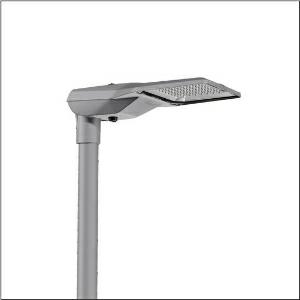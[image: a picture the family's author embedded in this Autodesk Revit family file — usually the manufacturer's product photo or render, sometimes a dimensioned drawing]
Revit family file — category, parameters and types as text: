
# Revit family: streetlight_sl_21_midi___st1_0a_5xe3d63t08nb_4f09
name_source: partatom
category: Lighting Fixtures
units: mm (PartAtom-declared; Revit-internal decimal feet)

## family parameters
Cut with Voids When Loaded = No
Host = Face
Light Source = No
Part Type = Normal
Room Calculation Point = No
Round Connector Dimension = Use Diameter
Shared = No

## types (1)
- --- (1 x LED, 20350 lm, 151.2 W, 2700K)
    Apparent Load = 151 VA
    CIE Flux Codes = 40 73 97 100 100
    Color Rendering = 70
    Color Temperature = 2700K
    Default Elevation = 1800 mm
    Description = Streetlight SL 21 midi, mast luminaire, primary light control with lens, of PMMA, primary optical cover: cover, of toughened safety glass, transparent, light distribution: ST1.0a, light emission: direct distribution, primary light characteristic: asymmetric, installation type: side-entry, post-top, LED, High Power LED, rated luminous flux: 20.350lm, luminous efficacy: 135lm/W, light colour: 727, colour temperature: 2700K, control gear: D4i, control: overheat protection, constant luminous flux control, time-dependent luminous flux control, flexible luminous flux parameterisation, pre-setting: logarithmic dimming characteristic, mains connection: 230..240V, AC, 50/60Hz, start of lifetime: 151W, end of service life: 157W, reduction: 70W, luminaire housing, of diecast aluminium, powder-coated, SITECO metallic grey (DB 702S), corrosivity category C5 high according to DIN EN ISO 12944, please order mast flange separately, inclination adjustable: 0°, 5°, 10°, 15°, sealing non-destructively replaceable, multi-level sealing system, length: 644mm, width: 335mm, height: 110mm, mast flange for spigot size: 42mm (side-entry): 5XC10008XM4, 60/48mm (side-entry/post-top): 5XC10108XM2, 76/60mm (side-entry/post-top): 5XC10108XM1, mounting height: 4..8m, Smart Interface below and above, protection rating (complete): IP66, insulation class (complete): insulation class II (safety insulation), certification: CE, ENEC, ENEC+, VDE, impact resistance: IK10, permissible operating ambient temperature for outdoor applications: -40..+50°C, standard-compliant lighting for roads and squares, packaging unit: 1 piece

Light Distribution: ST1.0a
    Height = 111 mm
    Lamp = 1 x LED
    Lamp Light Flux = 20350 lm
    Lamp Power = 151.2 W
    Lamp count = 1
    Length = 644 mm
    Luminous efficacy = 135 lm/W
    Manufacturer = Siteco
    ModVariant = No
    Model = 5XE3D63T08NB
    Number of Poles = 1
    OnlyDefault = Yes
    Power Factor = 1
    Product Name = Streetlight SL 21 midi | ST1.0a
    Product group = mast luminaire | pylon top
    ProductGroupID = 6100
    Protection Class = Protection class II
    Protection Degree = IP 66
    RLX_Detail_Level = 1
    RLX_Emergency_Light_Flux = 0 lm
    RLX_Emergency_Type = 0
    RLX_Emergency_Type_DB = No
    RlxData = <blob elided: 27129 chars, md5=f3806eff>
    Socket = socket
    Standby Power = 0 W
    System Light Flux = 20350 lm
    System Power = 151 W
    Type Comments = factory setting: luminous flux: 100 % | dim-lin: 254 | 802 mA
    Type Image = l_1004304.jpg
    URL = http://relux.com
    VarID = @adj_169901
    Voltage = 0 V
    Weight = 0.00 kg
    Width = 336 mm

## geometry (parser evidence)
native form markers: Blend x4, Sweep x11
no freeform markers — native parametric forms only
